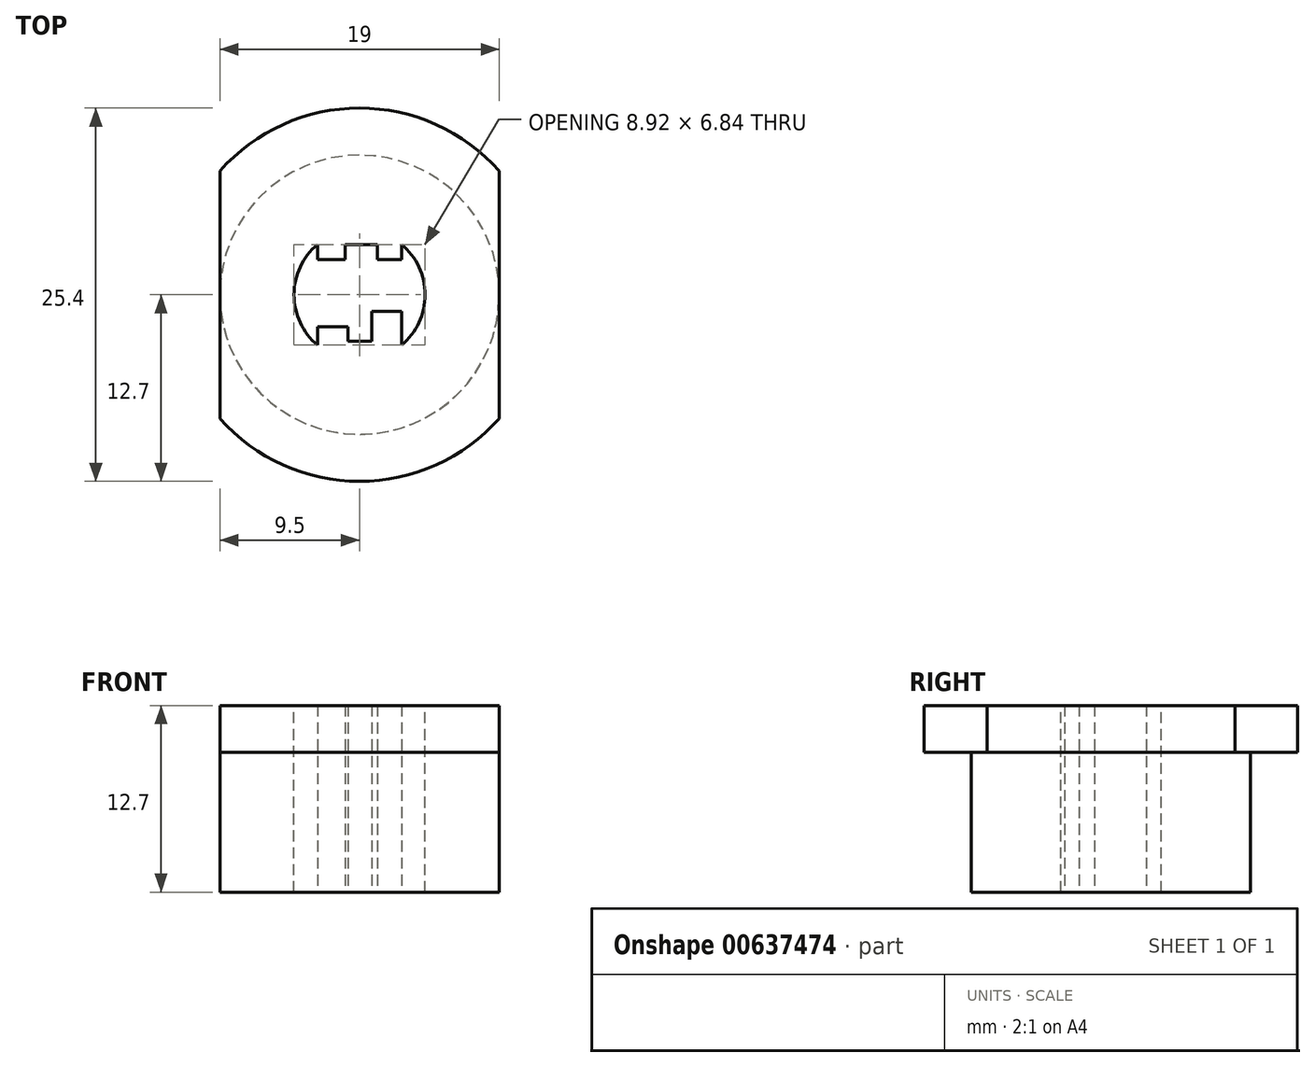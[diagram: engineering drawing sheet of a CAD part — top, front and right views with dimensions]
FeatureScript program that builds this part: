
annotation { "Feature Type Name" : "Feature", "Feature Type Description" : "" }
export const myFeature = defineFeature(function(context is Context, id is Id, definition is map)
    precondition{}
    {
        {
            var Q0;
            Q0=qCreatedBy(makeId("Top.planeOp"),FACE);
            var sketch = newSketch(context, id + "F0", { "sketchPlane" : qUnion([Q0])});
            skCircle(sketch, "E0", {"center": v(0, 0) * mm, "radius": 9.5 * mm});
            skSolve(sketch);
        }
        {
            var Q0;
            Q0=makeQuery(id+"F0.imprint","IMPRINT",FACE,{"disambiguationData":[TD([[makeQuery(id+"F0.imprint","IMPRINT",EDGE,{"derivedFrom":sQuery(id+"F0.wireOp",EDGE,"E0")}),1.0]])]});
            extrude(context, id + "F1", {"entities" : qUnion([Q0]), "depth" : 9.52 * mm, "offsetDistance" : 25.4 * mm});
        }
        {
            var Q0;
            Q0=makeQuery(id+"F1.opExtrude","CAP_FACE",FACE,{"disambiguationData":[OSD([sQuery(id+"F0.wireOp",EDGE,"E0")])],"isStart":false});
            var sketch = newSketch(context, id + "F2", { "sketchPlane" : qUnion([Q0])});
            skCircle(sketch, "E1", {"center": v(0, 0) * mm, "radius": 12.7 * mm});
            skSolve(sketch);
        }
        {
            var Q0;
            Q0=makeQuery(id+"F2.imprint","IMPRINT",FACE,{"disambiguationData":[TD([[makeQuery(id+"F2.imprint","IMPRINT",EDGE,{"derivedFrom":sQuery(id+"F2.wireOp",EDGE,"E1")}),1.0]])]});
            var Q1;
            Q1=makeQuery(id+"F2.imprint","IMPRINT",FACE,{"disambiguationData":[TD([[makeQuery(id+"F2.imprint","IMPRINT",EDGE,{"derivedFrom":makeQuery(id+"F1.opExtrude","CAP_EDGE",EDGE,{"disambiguationData":[OSD([sQuery(id+"F0.wireOp",EDGE,"E0")])],"isStart":false})}),1.0]])]});
            extrude(context, id + "F3", {"entities" : qUnion([Q0, Q1]), "operationType" : NewBodyOperationType.ADD, "depth" : 3.17 * mm, "offsetDistance" : 25.4 * mm});
        }
        {
            var Q0;
            Q0=makeQuery(id+"F3.opExtrude","CAP_FACE",FACE,{"disambiguationData":[OSD([sQuery(id+"F2.wireOp",EDGE,"E1")])],"isStart":false});
            var sketch = newSketch(context, id + "F4", { "sketchPlane" : qUnion([Q0])});
            skLineSegment(sketch, "E2", {"start": v(-9.5, -8.43) * mm, "end": v(-9.5, 8.43) * mm});
            skLineSegment(sketch, "E3", {"start": v(9.5, -8.43) * mm, "end": v(9.5, 8.43) * mm});
            skLineSegment(sketch, "E4", {"start": v(9.5, -8.43) * mm, "end": v(23.24, -8.43) * mm});
            skLineSegment(sketch, "E5", {"start": v(23.24, -8.43) * mm, "end": v(23.24, 8.67) * mm});
            skLineSegment(sketch, "E6", {"start": v(23.24, 8.67) * mm, "end": v(9.5, 8.43) * mm});
            skLineSegment(sketch, "E7", {"start": v(-9.5, -8.43) * mm, "end": v(-22.85, -8.43) * mm});
            skLineSegment(sketch, "E8", {"start": v(-22.85, -8.43) * mm, "end": v(-22.85, 8.43) * mm});
            skLineSegment(sketch, "E9", {"start": v(-22.85, 8.43) * mm, "end": v(-9.5, 8.43) * mm});
            skSolve(sketch);
        }
        {
            var Q0;
            {var subQ0=sQuery(id+"F4.wireOp",EDGE,"E2");Q0=makeQuery(id+"F4.imprint","IMPRINT",FACE,{"disambiguationData":[TD([[makeQuery(id+"F4.imprint","IMPRINT",EDGE,{"derivedFrom":subQ0}),1.0]])]});}
            var Q1;
            {var subQ0=sQuery(id+"F4.wireOp",EDGE,"E3");Q1=makeQuery(id+"F4.imprint","IMPRINT",FACE,{"disambiguationData":[TD([[makeQuery(id+"F4.imprint","IMPRINT",EDGE,{"derivedFrom":subQ0}),-1.0]])]});}
            extrude(context, id + "F5", {"entities" : qUnion([Q0, Q1]), "operationType" : NewBodyOperationType.REMOVE, "oppositeDirection" : true, "depth" : 25.4 * mm, "offsetDistance" : 25.4 * mm});
        }
        {
            var Q0;
            Q0=makeQuery(id+"F3.opExtrude","CAP_FACE",FACE,{"disambiguationData":[OSD([sQuery(id+"F2.wireOp",EDGE,"E1")])],"isStart":false});
            var sketch = newSketch(context, id + "F6", { "sketchPlane" : qUnion([Q0])});
            skCircle(sketch, "E10", {"center": v(0, 0) * mm, "radius": 4.46 * mm});
            skLineSegment(sketch, "E11", {"start": v(-2.86, 3.42) * mm, "end": v(-2.86, -3.42) * mm});
            skLineSegment(sketch, "E12", {"start": v(2.86, 3.42) * mm, "end": v(2.86, -3.42) * mm});
            skSolve(sketch);
        }
        {
            var Q0;
            {var subQ0=sQuery(id+"F6.wireOp",EDGE,"E12");Q0=makeQuery(id+"F6.imprint","IMPRINT",FACE,{"disambiguationData":[TD([[makeQuery(id+"F6.imprint","IMPRINT",EDGE,{"derivedFrom":subQ0}),1.0]])]});}
            var Q1;
            {var subQ0=sQuery(id+"F6.wireOp",EDGE,"E11");Q1=makeQuery(id+"F6.imprint","IMPRINT",FACE,{"disambiguationData":[TD([[makeQuery(id+"F6.imprint","IMPRINT",EDGE,{"derivedFrom":subQ0}),-1.0]])]});}
            extrude(context, id + "F7", {"entities" : qUnion([Q0, Q1]), "operationType" : NewBodyOperationType.REMOVE, "oppositeDirection" : true, "depth" : 25.4 * mm, "offsetDistance" : 25.4 * mm});
        }
        {
            var Q0;
            Q0=makeQuery(id+"F1.opExtrude","CAP_FACE",FACE,{"disambiguationData":[OSD([sQuery(id+"F0.wireOp",EDGE,"E0")])],"isStart":true});
            var sketch = newSketch(context, id + "F8", { "sketchPlane" : qUnion([Q0])});
            skCircle(sketch, "E13", {"center": v(0, 0) * mm, "radius": 4.46 * mm, "construction": true});
            skCircle(sketch, "E14", {"center": v(0, 2.67) * mm, "radius": 0.22 * mm, "construction": true});
            skCircle(sketch, "E15", {"center": v(-2.39, 1.65) * mm, "radius": 0.22 * mm, "construction": true});
            skCircle(sketch, "E16", {"center": v(-1.8, -1.8) * mm, "radius": 0.43 * mm, "construction": true});
            skCircle(sketch, "E17", {"center": v(0, -2.67) * mm, "radius": 0.22 * mm, "construction": true});
            skCircle(sketch, "E18", {"center": v(2.39, -1.65) * mm, "radius": 0.22 * mm, "construction": true});
            skLineSegment(sketch, "E19", {"start": v(-2.86, -2.4) * mm, "end": v(-0.97, -2.4) * mm});
            skLineSegment(sketch, "E20", {"start": v(-0.97, -2.4) * mm, "end": v(-0.97, -3.42) * mm});
            skLineSegment(sketch, "E21", {"start": v(-0.97, -3.42) * mm, "end": v(1.22, -3.42) * mm});
            skLineSegment(sketch, "E22", {"start": v(1.22, -3.42) * mm, "end": v(1.22, -2.4) * mm});
            skLineSegment(sketch, "E23", {"start": v(1.22, -2.4) * mm, "end": v(2.86, -2.4) * mm});
            skLineSegment(sketch, "E24", {"start": v(-2.86, 2.17) * mm, "end": v(-0.8, 2.17) * mm});
            skLineSegment(sketch, "E25", {"start": v(-0.8, 2.17) * mm, "end": v(-0.8, 3.16) * mm});
            skLineSegment(sketch, "E26", {"start": v(-0.8, 3.16) * mm, "end": v(0.83, 3.16) * mm});
            skLineSegment(sketch, "E27", {"start": v(0.83, 3.16) * mm, "end": v(0.83, 1.13) * mm});
            skLineSegment(sketch, "E28", {"start": v(0.83, 1.13) * mm, "end": v(2.86, 1.13) * mm});
            skLineSegment(sketch, "E29", {"start": v(2.86, -2.4) * mm, "end": v(2.86, 1.13) * mm});
            skLineSegment(sketch, "E30", {"start": v(-2.86, -2.4) * mm, "end": v(-2.86, 2.17) * mm});
            skSolve(sketch);
        }
        {
            var Q0;
            Q0 = qSketchRegion(id + "F8", true);
            extrude(context, id + "F9", {"entities" : qUnion([Q0]), "operationType" : NewBodyOperationType.REMOVE, "oppositeDirection" : true, "depth" : 25.4 * mm, "offsetDistance" : 25.4 * mm});
        }
    });
